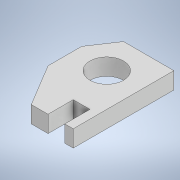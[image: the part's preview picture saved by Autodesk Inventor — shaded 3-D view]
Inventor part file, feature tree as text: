
AUTODESK INVENTOR PART (.ipt)
format: ipt  version: 2022.2 (Build 262287030, 287C)  size: 113,664 bytes
history: native  units: in
note: dims shown in document units (in); Inventor stores cm internally (conversion verified against a paired STEP export)
features: extrude x1, sketch x1
ambient origin geometry x8: Origin, YZ Plane, XZ Plane, XY Plane, X Axis, Y Axis, Z Axis, Center Point
bodies: Solid1 (feature_tree)
feature tree (2):
  extrude  "Extrusion1"  Depth=0.5in
  sketch  "Sketch1"  dims[d0=1.0in d1=1.0in d2=1.0in d3=0.75in d4=1.0in d5=1.5in d6=2.0in d8=1.25in d9=0.25in d10=0.75in d11=0.5in d12=3.0in d13=0.5in d14=0.0in]
